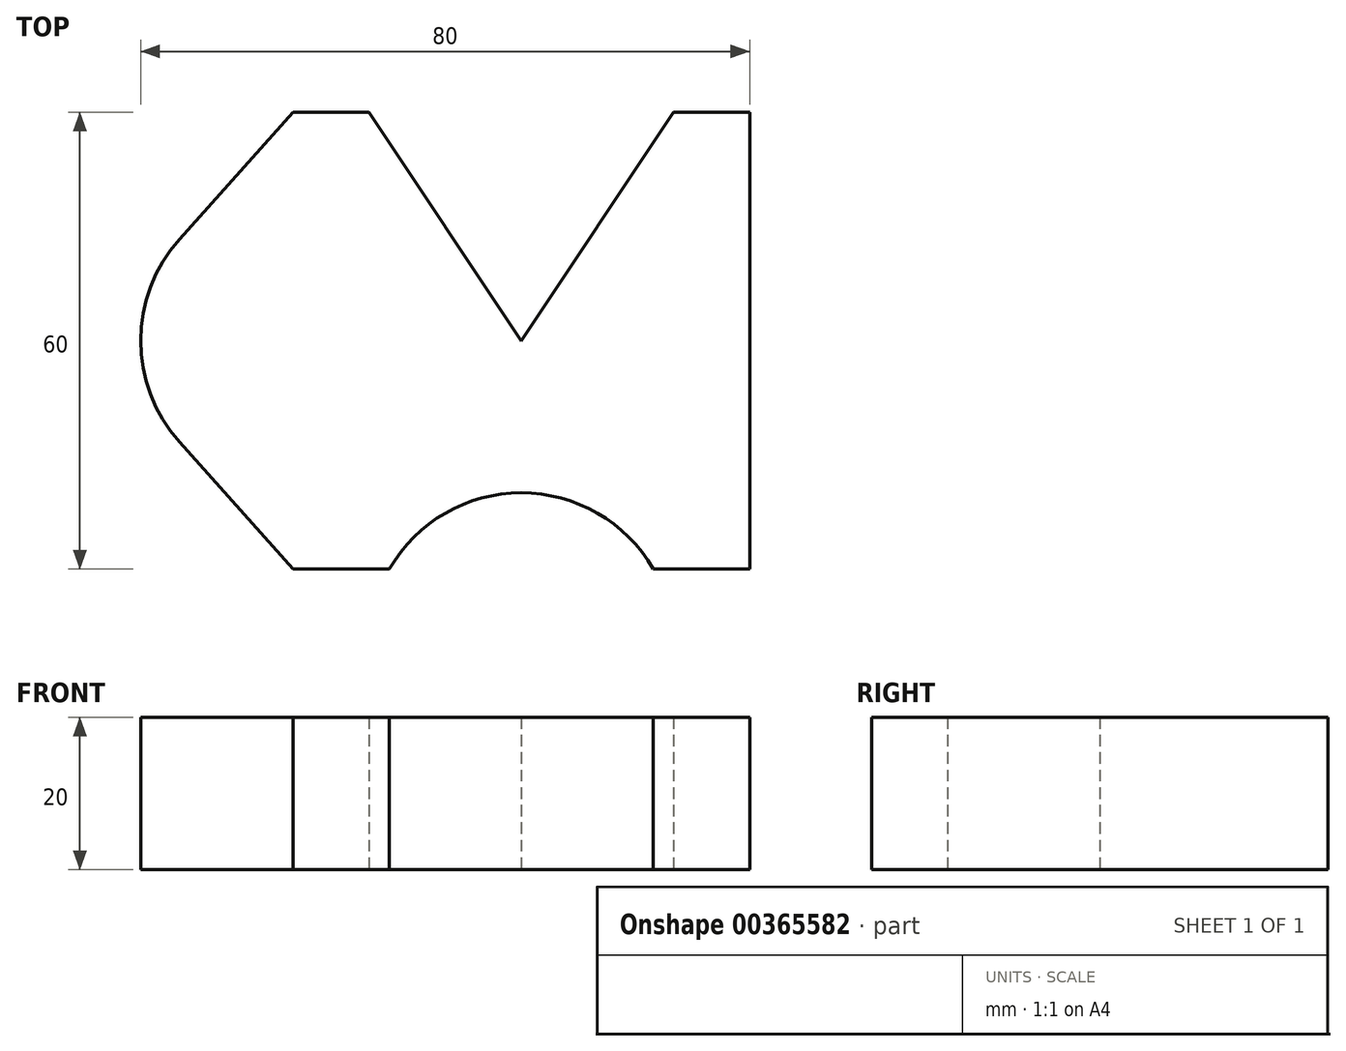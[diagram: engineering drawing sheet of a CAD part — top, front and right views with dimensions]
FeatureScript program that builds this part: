
annotation { "Feature Type Name" : "Feature", "Feature Type Description" : "" }
export const myFeature = defineFeature(function(context is Context, id is Id, definition is map)
    precondition{}
    {
        {
            var Q0;
            Q0=qCreatedBy(makeId("Top.planeOp"),FACE);
            var sketch = newSketch(context, id + "F0", { "sketchPlane" : qUnion([Q0])});
            skLineSegment(sketch, "E0", {"start": v(17.32, -30) * mm, "end": v(30, -30) * mm});
            skLineSegment(sketch, "E1", {"start": v(30, -30) * mm, "end": v(30, 30) * mm});
            skLineSegment(sketch, "E2", {"start": v(30, 30) * mm, "end": v(20, 30) * mm});
            skLineSegment(sketch, "E3", {"start": v(20, 30) * mm, "end": v(0, 0) * mm});
            skLineSegment(sketch, "E4", {"start": v(0, 0) * mm, "end": v(-20, 30) * mm});
            skLineSegment(sketch, "E5", {"start": v(-20, 30) * mm, "end": v(-30, 30) * mm});
            skLineSegment(sketch, "E6", {"start": v(-30, 30) * mm, "end": v(-44.9, 13.33) * mm});
            skArc(sketch, "E7", {"start": v(17.32, -30) * mm, "mid": v(0, -20) * mm, "end": v(-17.32, -30) * mm});
            skLineSegment(sketch, "E8", {"start": v(-17.32, -30) * mm, "end": v(-30, -30) * mm});
            skLineSegment(sketch, "E9", {"start": v(-30, -30) * mm, "end": v(-44.9, -13.33) * mm});
            skArc(sketch, "E10", {"start": v(-44.9, 13.33) * mm, "mid": v(-50, 0) * mm, "end": v(-44.9, -13.33) * mm});
            skLineSegment(sketch, "E11", {"start": v(-30, 30) * mm, "end": v(-30, -30) * mm, "construction": true});
            skSolve(sketch);
        }
        {
            var Q0;
            Q0=makeQuery(id+"F0.imprint","IMPRINT",FACE,{"disambiguationData":[TD([[makeQuery(id+"F0.imprint","IMPRINT",EDGE,{"derivedFrom":sQuery(id+"F0.wireOp",EDGE,"E0")}),1.0]])]});
            extrude(context, id + "F1", {"entities" : qUnion([Q0]), "depth" : 20 * mm});
        }
    });
